# Revit family: TY3531
name_source: partatom
category: Sprinklers
revit_build: Autodesk Revit 2016 (Build: 20150220_1215(x64)
units: mm (PartAtom-declared; Revit-internal decimal feet)

## family parameters
Always vertical = Yes
Cut with Voids When Loaded = No
Maintain Annotation Orientation = No
OmniClass Number = 23.65.70.17.11.24
OmniClass Title = Fire Fighting Sprinkler Heads
Part Type = Normal
Room Calculation Point = No
Round Connector Dimension = Use Diameter
Shared = No
Work Plane-Based = No

## types (7) — shared parameters
COBie = Yes
COBie.Component.Description = RFII Concealed Flush SC QR/SR 200°F K5.6 1/2 NPT
COBie.Component.Name = Sprinklers:Concealed Flush
COBie.Type = Yes
COBie.Type.AssetType = Fixed
COBie.Type.Category = Pr_70_55_97_84:Sprinklers
COBie.Type.DurationUnit = year
COBie.Type.Manufacturer = Tyco Fire Protection Products
COBie.Type.Material = Bronze
COBie.Type.ModelReference = RFII Concealed Flush SC QR/SR 200°F K5.6 1/2 NPT
COBie.Type.Shape = Cylinder
COBie.Type.Size = 1/2"(DN15)
COBie.Type.WarrantyGuarantorParts = http://tycofsbp.com
Coverage = Standard
Coverage_ = Standard
Description = Tyco RF II Pendent K5.6/80 93°C 1/2"/DN15 NPT Brass Plated TY3531
K-Factor = 80.64
Manufacturer = Tyco Fire Protection Products
Manufacturer URL = www.tyco-fire.com
Material_ = Bronze
Model = RFII
Nominal Diameter 1 = 15 mm
Orifice = Extra Large
Orifice Size = 0 mm
Outside Diameter 1 = 21 mm
Response = Quick
Response_ = Quick
SIN No = TY3531
Takeout 1 = 62 mm
Technical Data Sheet = TFP181
Temperature Rating = 93 °C
zero-valued in all types: COBie.Type.NominalHeight, COBie.Type.NominalLength, COBie.Type.NominalWidth, COBie.Type.ReplacementCost, Style Id

## per-type parameters (varying)
| type | COBie.Type.Finish | COBie.Type.ModelNumber | Finish_ | Part No |
| RFll Concealed Pendent 68°C 1/2" NPT Signal White_51-792-4-155 | Signal White | 51-792-4-155 | Signal White | 51-792-4-155 |
| RFll Concealed Pendent 93°C 1/2" NPT Brass_51-792-1-200 | Brass | 51-792-1-200 | Natural Brass | 51-792-1-200 |
| RFll Concealed Pendent 93°C 1/2" NPT Pure White_51-792-3-155 | Pure White | 51-792-3-155 | Pure White | 51-792-3-155 |
| RFll Concealed Pendent 93°C 1/2" NPT Chrome_51-792-9-155 | Chrome | 51-792-9-155 | Chrome | 51-792-9-155 |
| RFll Concealed Pendent 68°C 1/2" NPT Gray White_51-792-0-155 | Gray White | 51-792-0-155 | Gray White | 51-792-0-155 |
| RFll Concealed Pendent 68°C 1/2" NPT Jet Black_51-792-6-155 | Jet Black | 51-792-6-155 | Jet Black | 51-792-6-155 |
| RFll Concealed Pendent 68°C 1/2" NPT Chrome_51-792-8-155 | Chrome | 51-792-8-155 | Chrome | 51-792-8-155 |

## geometry (parser evidence)
native form markers: Blend x2, Sweep x36
no freeform markers — native parametric forms only
